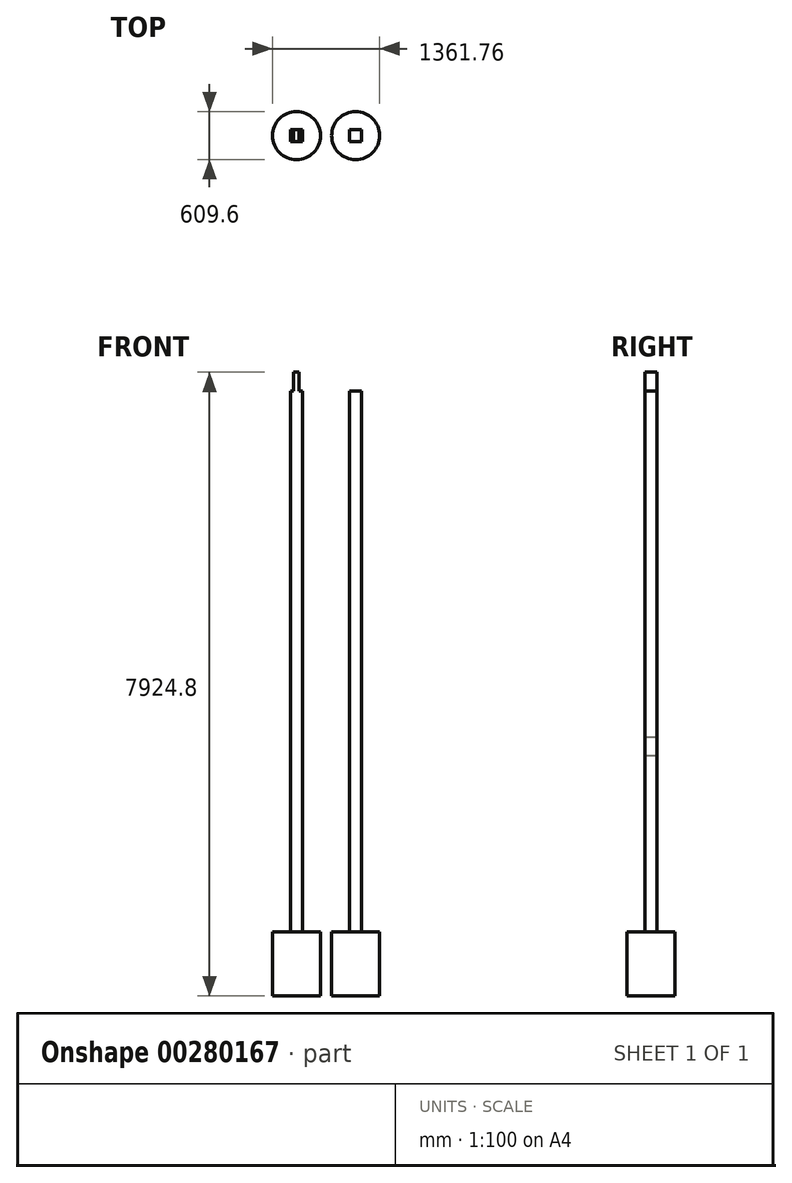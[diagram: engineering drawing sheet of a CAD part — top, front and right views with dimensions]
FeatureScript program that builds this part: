
annotation { "Feature Type Name" : "Feature", "Feature Type Description" : "" }
export const myFeature = defineFeature(function(context is Context, id is Id, definition is map)
    precondition{}
    {
        {
            var Q0;
            Q0=qCreatedBy(makeId("Top.planeOp"),FACE);
            var sketch = newSketch(context, id + "F0", { "sketchPlane" : qUnion([Q0])});
            skCircle(sketch, "E0", {"center": v(0, 0) * mm, "radius": 304.8 * mm});
            skCircle(sketch, "E1", {"center": v(752.16, 0) * mm, "radius": 304.8 * mm});
            skSolve(sketch);
        }
        {
            var Q0;
            Q0=makeQuery(id+"F0.imprint","IMPRINT",FACE,{"disambiguationData":[TD([[makeQuery(id+"F0.imprint","IMPRINT",EDGE,{"derivedFrom":sQuery(id+"F0.wireOp",EDGE,"E0")}),1.0]])]});
            var Q1;
            Q1=makeQuery(id+"F0.imprint","IMPRINT",FACE,{"disambiguationData":[TD([[makeQuery(id+"F0.imprint","IMPRINT",EDGE,{"derivedFrom":sQuery(id+"F0.wireOp",EDGE,"E1")}),1.0]])]});
            extrude(context, id + "F1", {"entities" : qUnion([Q0, Q1]), "depth" : 7924.8 * mm});
        }
        {
            var Q0;
            Q0=makeQuery(id+"F1.opExtrude","CAP_FACE",FACE,{"disambiguationData":[OSD([sQuery(id+"F0.wireOp",EDGE,"E0")])],"isStart":false});
            var sketch = newSketch(context, id + "F2", { "sketchPlane" : qUnion([Q0])});
            skLineSegment(sketch, "E2.bottom", {"start": v(76.2, -76.2) * mm, "end": v(-76.2, -76.2) * mm});
            skLineSegment(sketch, "E2.top", {"start": v(76.2, 76.2) * mm, "end": v(-76.2, 76.2) * mm});
            skLineSegment(sketch, "E2.left", {"start": v(76.2, -76.2) * mm, "end": v(76.2, 76.2) * mm});
            skLineSegment(sketch, "E2.right", {"start": v(-76.2, -76.2) * mm, "end": v(-76.2, 76.2) * mm});
            skPoint(sketch, "E2.middle", {"position": v(0, 0) * mm});
            skSolve(sketch);
        }
        {
            var Q0;
            Q0=makeQuery(id+"F2.imprint","IMPRINT",FACE,{"disambiguationData":[TD([[makeQuery(id+"F2.imprint","IMPRINT",EDGE,{"derivedFrom":sQuery(id+"F2.wireOp",EDGE,"E2.bottom")}),1.0]])]});
            extrude(context, id + "F3", {"entities" : qUnion([Q0]), "operationType" : NewBodyOperationType.REMOVE, "oppositeDirection" : true, "depth" : 7111.9 * mm});
        }
        {
            var Q0;
            Q0=makeQuery(id+"F1.opExtrude","CAP_FACE",FACE,{"disambiguationData":[OSD([sQuery(id+"F0.wireOp",EDGE,"E0")])],"isStart":false});
            var sketch = newSketch(context, id + "F4", { "sketchPlane" : qUnion([Q0])});
            skLineSegment(sketch, "E3", {"start": v(-34.93, 76.2) * mm, "end": v(-34.92, -76.2) * mm});
            skLineSegment(sketch, "E4", {"start": v(34.92, 76.2) * mm, "end": v(34.93, -76.2) * mm});
            skSolve(sketch);
        }
        {
            var Q0;
            {var subQ0=sQuery(id+"F4.wireOp",EDGE,"E3");Q0=makeQuery(id+"F4.imprint","IMPRINT",FACE,{"disambiguationData":[TD([[makeQuery(id+"F4.imprint","IMPRINT",EDGE,{"derivedFrom":subQ0}),-1.0]])]});}
            var Q1;
            {var subQ0=sQuery(id+"F4.wireOp",EDGE,"E4");Q1=makeQuery(id+"F4.imprint","IMPRINT",FACE,{"disambiguationData":[TD([[makeQuery(id+"F4.imprint","IMPRINT",EDGE,{"derivedFrom":subQ0}),1.0]])]});}
            extrude(context, id + "F5", {"entities" : qUnion([Q0, Q1]), "operationType" : NewBodyOperationType.REMOVE, "oppositeDirection" : true, "depth" : 241.3 * mm});
        }
        {
            var Q0;
            Q0=makeQuery(id+"F1.opExtrude","CAP_FACE",FACE,{"disambiguationData":[OSD([sQuery(id+"F0.wireOp",EDGE,"E1")])],"isStart":false});
            var sketch = newSketch(context, id + "F6", { "sketchPlane" : qUnion([Q0])});
            skLineSegment(sketch, "E5.bottom", {"start": v(828.36, -76.2) * mm, "end": v(675.96, -76.2) * mm});
            skLineSegment(sketch, "E5.top", {"start": v(828.36, 76.2) * mm, "end": v(675.96, 76.2) * mm});
            skLineSegment(sketch, "E5.left", {"start": v(828.36, -76.2) * mm, "end": v(828.36, 76.2) * mm});
            skLineSegment(sketch, "E5.right", {"start": v(675.96, -76.2) * mm, "end": v(675.96, 76.2) * mm});
            skPoint(sketch, "E5.middle", {"position": v(752.16, 0) * mm});
            skSolve(sketch);
        }
        {
            var Q0;
            Q0=makeQuery(id+"F6.imprint","IMPRINT",FACE,{"disambiguationData":[TD([[makeQuery(id+"F6.imprint","IMPRINT",EDGE,{"derivedFrom":sQuery(id+"F6.wireOp",EDGE,"E5.bottom")}),1.0]])]});
            extrude(context, id + "F7", {"entities" : qUnion([Q0]), "operationType" : NewBodyOperationType.REMOVE, "oppositeDirection" : true, "depth" : 7111.9 * mm});
        }
        {
            var Q0;
            Q0=makeQuery(id+"F1.opExtrude","CAP_FACE",FACE,{"disambiguationData":[OSD([sQuery(id+"F0.wireOp",EDGE,"E1")])],"isStart":false});
            var sketch = newSketch(context, id + "F8", { "sketchPlane" : qUnion([Q0])});
            skLineSegment(sketch, "E6", {"start": v(717.23, 76.2) * mm, "end": v(717.23, -76.2) * mm});
            skLineSegment(sketch, "E7", {"start": v(675.96, -35.05) * mm, "end": v(828.36, -35.05) * mm});
            skLineSegment(sketch, "E8", {"start": v(787.21, -76.2) * mm, "end": v(787.21, 76.2) * mm});
            skLineSegment(sketch, "E9", {"start": v(675.96, 35.05) * mm, "end": v(828.36, 35.05) * mm});
            skSolve(sketch);
        }
        {
            var Q0;
            {var subQ0=sQuery(id+"F8.wireOp",EDGE,"E6");var subQ1=makeQuery(id+"F7.boolean.opBoolean","COPY",EDGE,{"derivedFrom":makeQuery(id+"F7.opExtrude","CAP_EDGE",EDGE,{"disambiguationData":[OSD([sQuery(id+"F6.wireOp",EDGE,"E5.top")])],"isStart":true})});var subQ2=makeQuery(id+"F8.imprint","INTERSECT",VERTEX,{"derivedFrom":[subQ1,subQ0]});Q0=makeQuery(id+"F8.imprint","IMPRINT",FACE,{"disambiguationData":[TD([[makeQuery(id+"F8.imprint","IMPRINT",EDGE,{"disambiguationData":[TD([[subQ2,-1.0]])],"derivedFrom":subQ0}),-1.0]])]});}
            var Q1;
            {var subQ0=sQuery(id+"F8.wireOp",EDGE,"E6");var subQ1=makeQuery(id+"F7.boolean.opBoolean","COPY",EDGE,{"derivedFrom":makeQuery(id+"F7.opExtrude","CAP_EDGE",EDGE,{"disambiguationData":[OSD([sQuery(id+"F6.wireOp",EDGE,"E5.bottom")])],"isStart":true})});var subQ2=makeQuery(id+"F8.imprint","INTERSECT",VERTEX,{"derivedFrom":[subQ1,subQ0]});Q1=makeQuery(id+"F8.imprint","IMPRINT",FACE,{"disambiguationData":[TD([[makeQuery(id+"F8.imprint","IMPRINT",EDGE,{"disambiguationData":[TD([[subQ2,1.0]])],"derivedFrom":subQ0}),-1.0]])]});}
            var Q2;
            {var subQ0=sQuery(id+"F8.wireOp",EDGE,"E6");var subQ1=makeQuery(id+"F7.boolean.opBoolean","COPY",EDGE,{"derivedFrom":makeQuery(id+"F7.opExtrude","CAP_EDGE",EDGE,{"disambiguationData":[OSD([sQuery(id+"F6.wireOp",EDGE,"E5.bottom")])],"isStart":true})});var subQ2=makeQuery(id+"F8.imprint","INTERSECT",VERTEX,{"derivedFrom":[subQ1,subQ0]});Q2=makeQuery(id+"F8.imprint","IMPRINT",FACE,{"disambiguationData":[TD([[makeQuery(id+"F8.imprint","IMPRINT",EDGE,{"disambiguationData":[TD([[subQ2,1.0]])],"derivedFrom":subQ0}),1.0]])]});}
            var Q3;
            {var subQ0=sQuery(id+"F8.wireOp",EDGE,"E9");var subQ1=sQuery(id+"F8.wireOp",EDGE,"E6");var subQ2=makeQuery(id+"F8.imprint","INTERSECT",VERTEX,{"derivedFrom":[subQ1,subQ0]});Q3=makeQuery(id+"F8.imprint","IMPRINT",FACE,{"disambiguationData":[TD([[makeQuery(id+"F8.imprint","IMPRINT",EDGE,{"disambiguationData":[TD([[subQ2,-1.0]])],"derivedFrom":subQ1}),-1.0]])]});}
            var Q4;
            {var subQ0=sQuery(id+"F8.wireOp",EDGE,"E6");var subQ1=makeQuery(id+"F7.boolean.opBoolean","COPY",EDGE,{"derivedFrom":makeQuery(id+"F7.opExtrude","CAP_EDGE",EDGE,{"disambiguationData":[OSD([sQuery(id+"F6.wireOp",EDGE,"E5.top")])],"isStart":true})});var subQ2=makeQuery(id+"F8.imprint","INTERSECT",VERTEX,{"derivedFrom":[subQ1,subQ0]});Q4=makeQuery(id+"F8.imprint","IMPRINT",FACE,{"disambiguationData":[TD([[makeQuery(id+"F8.imprint","IMPRINT",EDGE,{"disambiguationData":[TD([[subQ2,-1.0]])],"derivedFrom":subQ0}),1.0]])]});}
            var Q5;
            {var subQ0=sQuery(id+"F8.wireOp",EDGE,"E8");var subQ1=makeQuery(id+"F7.boolean.opBoolean","COPY",EDGE,{"derivedFrom":makeQuery(id+"F7.opExtrude","CAP_EDGE",EDGE,{"disambiguationData":[OSD([sQuery(id+"F6.wireOp",EDGE,"E5.top")])],"isStart":true})});var subQ2=makeQuery(id+"F8.imprint","INTERSECT",VERTEX,{"derivedFrom":[subQ1,subQ0]});Q5=makeQuery(id+"F8.imprint","IMPRINT",FACE,{"disambiguationData":[TD([[makeQuery(id+"F8.imprint","IMPRINT",EDGE,{"disambiguationData":[TD([[subQ2,1.0]])],"derivedFrom":subQ0}),-1.0]])]});}
            var Q6;
            {var subQ0=sQuery(id+"F8.wireOp",EDGE,"E7");var subQ1=makeQuery(id+"F7.boolean.opBoolean","COPY",EDGE,{"derivedFrom":makeQuery(id+"F7.opExtrude","CAP_EDGE",EDGE,{"disambiguationData":[OSD([sQuery(id+"F6.wireOp",EDGE,"E5.left")])],"isStart":true})});var subQ2=makeQuery(id+"F8.imprint","INTERSECT",VERTEX,{"derivedFrom":[subQ1,subQ0]});Q6=makeQuery(id+"F8.imprint","IMPRINT",FACE,{"disambiguationData":[TD([[makeQuery(id+"F8.imprint","IMPRINT",EDGE,{"disambiguationData":[TD([[subQ2,1.0]])],"derivedFrom":subQ0}),1.0]])]});}
            var Q7;
            {var subQ0=sQuery(id+"F8.wireOp",EDGE,"E7");var subQ1=makeQuery(id+"F7.boolean.opBoolean","COPY",EDGE,{"derivedFrom":makeQuery(id+"F7.opExtrude","CAP_EDGE",EDGE,{"disambiguationData":[OSD([sQuery(id+"F6.wireOp",EDGE,"E5.left")])],"isStart":true})});var subQ2=makeQuery(id+"F8.imprint","INTERSECT",VERTEX,{"derivedFrom":[subQ1,subQ0]});Q7=makeQuery(id+"F8.imprint","IMPRINT",FACE,{"disambiguationData":[TD([[makeQuery(id+"F8.imprint","IMPRINT",EDGE,{"disambiguationData":[TD([[subQ2,1.0]])],"derivedFrom":subQ0}),-1.0]])]});}
            extrude(context, id + "F9", {"entities" : qUnion([Q0, Q1, Q2, Q3, Q4, Q5, Q6, Q7]), "operationType" : NewBodyOperationType.REMOVE, "oppositeDirection" : true, "depth" : 241.3 * mm});
        }
        {
            var Q0;
            Q0=makeQuery(id+"F3.boolean.opBoolean","COPY",FACE,{"derivedFrom":makeQuery(id+"F3.opExtrude","SWEPT_FACE",FACE,{"disambiguationData":[OSD([sQuery(id+"F2.wireOp",EDGE,"E2.left")])]})});
            var sketch = newSketch(context, id + "F10", { "sketchPlane" : qUnion([Q0])});
            skLineSegment(sketch, "E10.bottom", {"start": v(-76.2, 3289.3) * mm, "end": v(76.2, 3289.3) * mm});
            skLineSegment(sketch, "E10.top", {"start": v(-76.2, 3048) * mm, "end": v(76.2, 3048) * mm});
            skLineSegment(sketch, "E10.left", {"start": v(-76.2, 3289.3) * mm, "end": v(-76.2, 3048) * mm});
            skLineSegment(sketch, "E10.right", {"start": v(76.2, 3289.3) * mm, "end": v(76.2, 3048) * mm});
            skSolve(sketch);
        }
        {
            var Q0;
            Q0=makeQuery(id+"F3.boolean.opBoolean","COPY",FACE,{"derivedFrom":makeQuery(id+"F3.opExtrude","SWEPT_FACE",FACE,{"disambiguationData":[OSD([sQuery(id+"F2.wireOp",EDGE,"E2.right")])]})});
            var sketch = newSketch(context, id + "F11", { "sketchPlane" : qUnion([Q0])});
            skLineSegment(sketch, "E11.bottom", {"start": v(-76.2, 3048) * mm, "end": v(76.2, 3048) * mm});
            skLineSegment(sketch, "E11.top", {"start": v(-76.2, 3289.3) * mm, "end": v(76.2, 3289.3) * mm});
            skLineSegment(sketch, "E11.left", {"start": v(-76.2, 3048) * mm, "end": v(-76.2, 3289.3) * mm});
            skLineSegment(sketch, "E11.right", {"start": v(76.2, 3048) * mm, "end": v(76.2, 3289.3) * mm});
            skSolve(sketch);
        }
        {
            var Q0;
            Q0=makeQuery(id+"F11.imprint","IMPRINT",FACE,{"disambiguationData":[TD([[makeQuery(id+"F11.imprint","IMPRINT",EDGE,{"derivedFrom":sQuery(id+"F11.wireOp",EDGE,"E11.bottom")}),1.0]])]});
            extrude(context, id + "F12", {"entities" : qUnion([Q0]), "operationType" : NewBodyOperationType.REMOVE, "oppositeDirection" : true, "depth" : 0.3 * mm});
        }
        {
            var Q0;
            Q0=makeQuery(id+"F10.imprint","IMPRINT",FACE,{"disambiguationData":[TD([[makeQuery(id+"F10.imprint","IMPRINT",EDGE,{"derivedFrom":sQuery(id+"F10.wireOp",EDGE,"E10.bottom")}),-1.0]])]});
            extrude(context, id + "F13", {"entities" : qUnion([Q0]), "operationType" : NewBodyOperationType.REMOVE, "oppositeDirection" : true, "depth" : 0.3 * mm});
        }
    });
